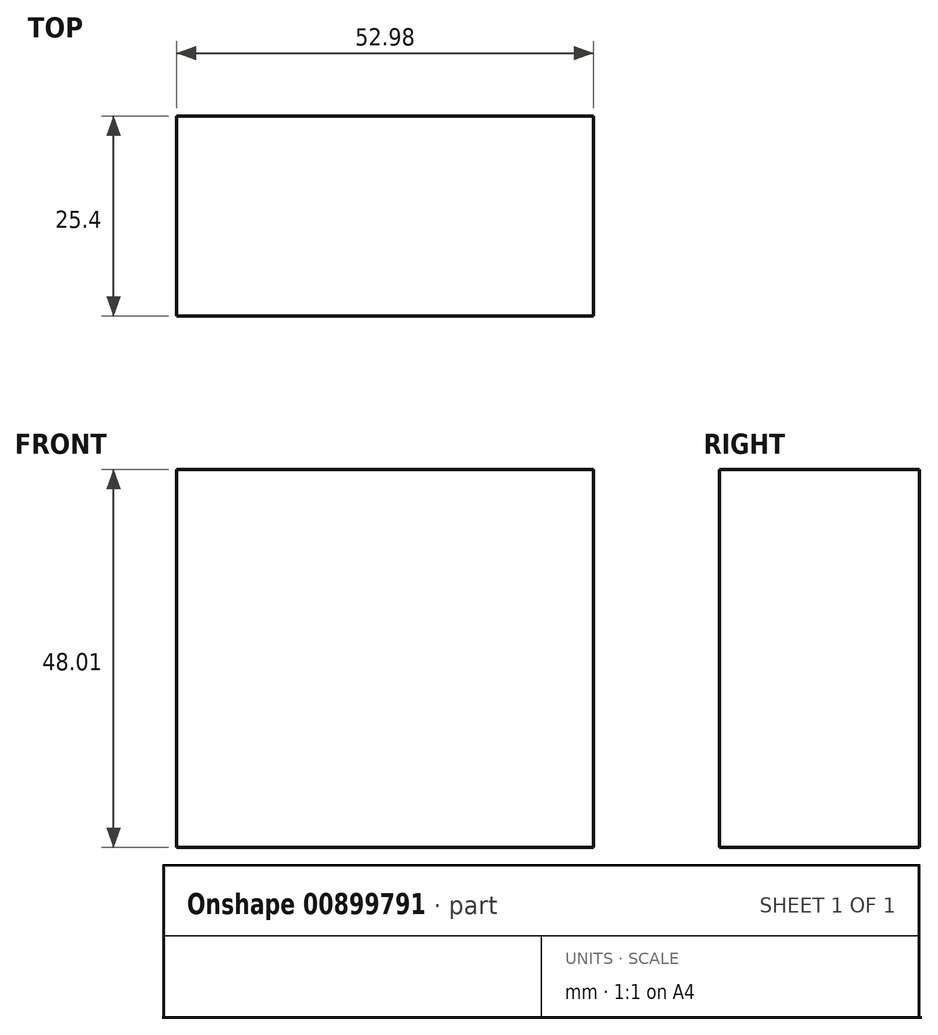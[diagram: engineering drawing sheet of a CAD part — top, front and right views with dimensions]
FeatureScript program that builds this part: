
annotation { "Feature Type Name" : "Feature", "Feature Type Description" : "" }
export const myFeature = defineFeature(function(context is Context, id is Id, definition is map)
    precondition{}
    {
        {
            var Q0;
            Q0=qCreatedBy(makeId("Front.planeOp"),FACE);
            var sketch = newSketch(context, id + "F0", { "sketchPlane" : qUnion([Q0])});
            skLineSegment(sketch, "E0.bottom", {"start": v(-13.66, 8.7) * mm, "end": v(39.32, 8.7) * mm});
            skLineSegment(sketch, "E0.top", {"start": v(-13.66, -39.32) * mm, "end": v(39.32, -39.32) * mm});
            skLineSegment(sketch, "E0.left", {"start": v(-13.66, 8.7) * mm, "end": v(-13.66, -39.32) * mm});
            skLineSegment(sketch, "E0.right", {"start": v(39.32, 8.7) * mm, "end": v(39.32, -39.32) * mm});
            skSolve(sketch);
        }
        {
            var Q0;
            Q0 = qSketchRegion(id + "F0", true);
            extrude(context, id + "F1", {"entities" : qUnion([Q0]), "depth" : 25.4 * mm, "offsetDistance" : 25.4 * mm});
        }
    });
